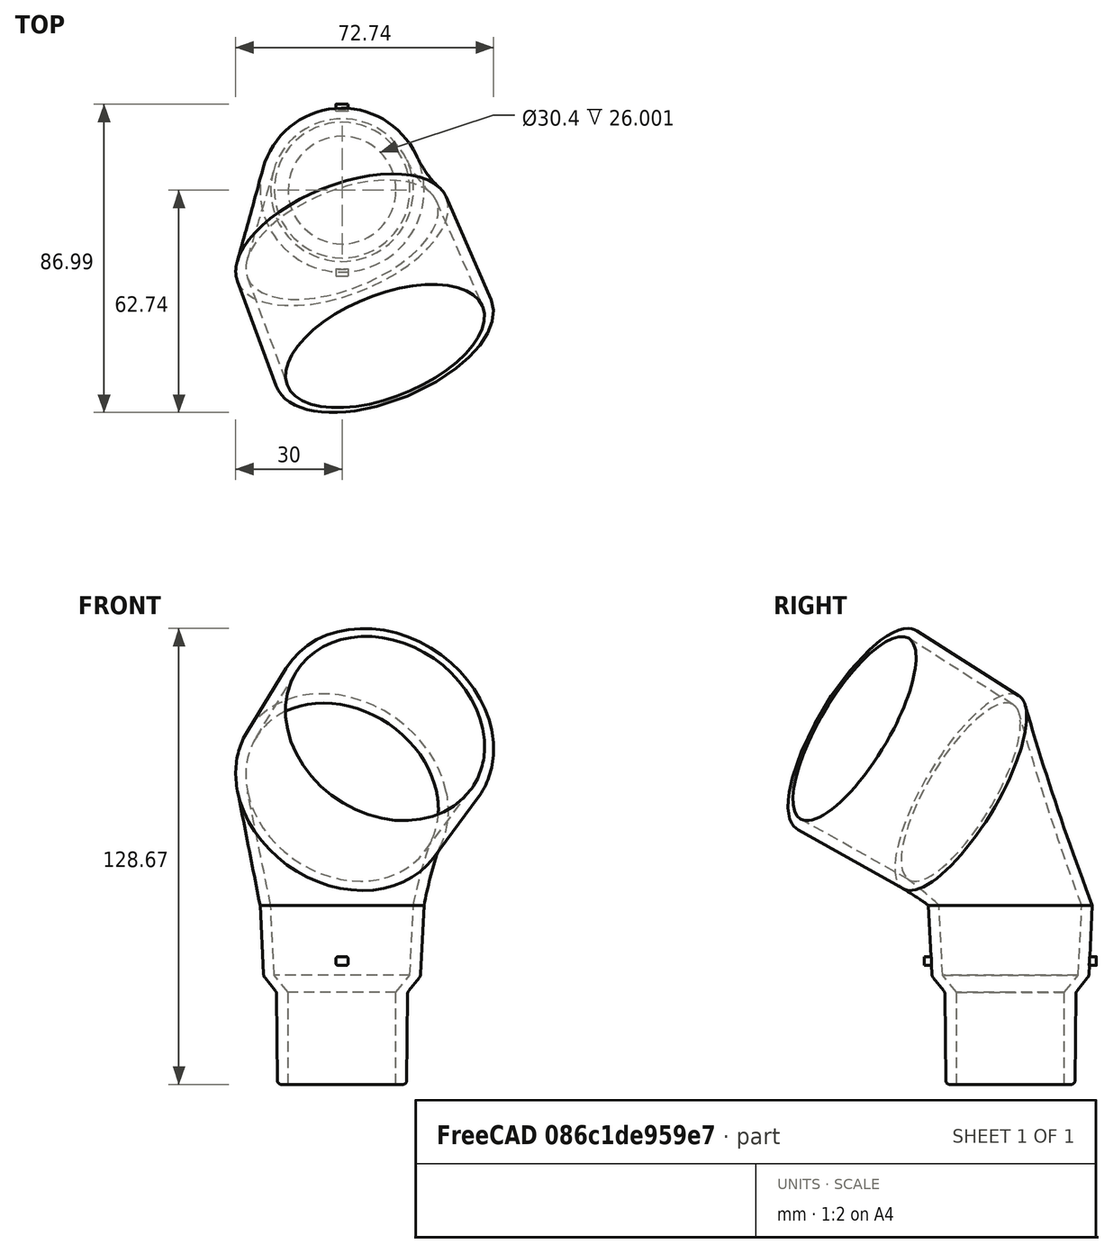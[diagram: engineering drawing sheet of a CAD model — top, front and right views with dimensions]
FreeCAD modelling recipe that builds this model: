
FCSTD DOCUMENT  (FreeCAD 1.1R20260414 (Git shallow))
Label: M18Vac
License: All rights reserved
LicenseURL: http://en.wikipedia.org/wiki/All_rights_reserved
objects: Sketcher::SketchObject×4, App::Point×2, PartDesign::Pad×2, Part::DatumPlane×2, PartDesign::Fillet×2, Spreadsheet::Sheet×1, PartDesign::Revolution×1, PartDesign::PolarPattern×1, PartDesign::AdditiveLoft×1, PartDesign::Body×1, App::Part×1, Mesh::Feature×1
note: 29 computed .brp shape members not serialized (recipe doc carries the construction recipe); baked Part::Feature solids carry a one-line shape summary decoded from their .brp

FEATURE [App::Point] Origin001
  Role = Origin
FEATURE [App::Point] Origin003
  Role = Origin
FEATURE [Sketcher::SketchObject] Sketch  label="Sketch-Plug"
  ArcFitTolerance = 1e-06
  AttachmentSupport = -> [Origin002]
  ExternalTypes = [0]
  FullyConstrained = true
  MakeInternals = false
  MapMode = 5
  Placement = pos=(0,0,0) rot=(1,0,0;1.5708rad)
  _ExternalGeoVersion = 1
  expr: Constraints[10] = Spreadsheet.Neck / 2
  expr: Constraints[16] = Spreadsheet.Thickness
  expr: Constraints[3] = 36.4 / 2
  expr: Constraints[4] = Spreadsheet.Thickness
  expr: Constraints[6] = 36.9 / 2
  expr: Constraints[8] = 44.25 / 2
  sketch-geometry (8):
    g0: LineSegment StartX=18.2 StartY=0 StartZ=0 EndX=18.45 EndY=26 EndZ=0
    g1: LineSegment StartX=22.125 StartY=30.5 StartZ=0 EndX=23.125 EndY=50.5 EndZ=0
    g2: LineSegment StartX=15.2 StartY=0 StartZ=0 EndX=18.2 EndY=0 EndZ=0
    g3: LineSegment StartX=15.2 StartY=0 StartZ=0 EndX=15.2 EndY=26.0012 EndZ=0
    g4: LineSegment StartX=19.1414 StartY=30.8274 StartZ=0 EndX=20.125 EndY=50.5 EndZ=0
    g5: LineSegment StartX=20.125 StartY=50.5 StartZ=0 EndX=23.125 EndY=50.5 EndZ=0
    g6: LineSegment StartX=15.2 StartY=26.0012 StartZ=0 EndX=19.1414 EndY=30.8274 EndZ=0
    g7: LineSegment StartX=18.45 StartY=26 StartZ=0 EndX=22.125 EndY=30.5 EndZ=0
  constraints (24):
    c: PointOnObject(g0,g-1)
    c: Coincident(g2,g0)
    c: Horizontal(g2)
    c: DistanceX(g-1,g0) = 18.2
    c: Distance(g2) = 3
    c: DistanceY(g0,g0) = 26
    c: DistanceX(g-1,g0) = 18.45
    c: DistanceY(g0,g1) = 4.5
    c: DistanceX(g-1,g1) = 22.125
    c: DistanceY(g1,g1) = 20
    c: DistanceX(g-1,g1) = 23.125
    c: Coincident(g3,g2)
    c: Vertical(g3)
    c: Coincident(g5,g1)
    c: Coincident(g4,g5)
    c: Equal(g3,g0)
    c: DistanceX(g5,g5) = 3
    c: Coincident(g6,g3)
    c: Coincident(g6,g4)
    c: Coincident(g7,g0)
    c: Coincident(g7,g1)
    c: Parallel(g1,g4)
    c: Parallel(g6,g7)
    c: Horizontal(g5)
FEATURE [Spreadsheet::Sheet] Spreadsheet
  cells = A2='Thickness; B2(Thickness)=3; A4='Neck; B4(Neck)=46.25; A9='HoseInsideDia; B9(HoseInsideDia)=57.5; A10='HoseLength; B10(HoseLength)=37
FEATURE [PartDesign::Revolution] Revolution
  Angle = 360
  Angle2 = 0
  Axis = (0,2e-16,1)
  Base = (0,0,0)
  FuseOrder = 0
  Profile = -> Sketch
  ReferenceAxis = -> Sketch [V_Axis]
  Reversed = true
  Suppressed = false
  Type = 0
FEATURE [Sketcher::SketchObject] Sketch001  label="Sketch-Pin"
  ArcFitTolerance = 1e-06
  AttachmentOffset = pos=(0,34.8,22) rot=(0,0,1;0rad)
  AttachmentSupport = -> [Origin002]
  ExternalTypes = [0]
  FullyConstrained = true
  MakeInternals = false
  MapMode = 5
  Placement = pos=(0,-22,34.8) rot=(1,0,0;1.5708rad)
  _ExternalGeoVersion = 1
  sketch-geometry (10):
    g0: LineSegment StartX=-1.75 StartY=0.55 StartZ=0 EndX=-1.75 EndY=-0.55 EndZ=0
    g1: LineSegment StartX=-1.05 StartY=-1.25 StartZ=0 EndX=1.05 EndY=-1.25 EndZ=0
    g2: LineSegment StartX=1.75 StartY=-0.55 StartZ=0 EndX=1.75 EndY=0.55 EndZ=0
    g3: LineSegment StartX=1.05 StartY=1.25 StartZ=0 EndX=-1.05 EndY=1.25 EndZ=0
    g4: ArcOfCircle CenterX=-1.05 CenterY=0.55 CenterZ=0 NormalX=0 NormalY=0 NormalZ=1 AngleXU=0 Radius=0.7 StartAngle=1.5708 EndAngle=3.14159
    g5: ArcOfCircle CenterX=-1.05 CenterY=-0.55 CenterZ=0 NormalX=0 NormalY=0 NormalZ=1 AngleXU=0 Radius=0.7 StartAngle=3.14159 EndAngle=4.71239
    g6: ArcOfCircle CenterX=1.05 CenterY=-0.55 CenterZ=0 NormalX=0 NormalY=0 NormalZ=1 AngleXU=0 Radius=0.7 StartAngle=4.71239 EndAngle=6.28319
    g7: ArcOfCircle CenterX=1.05 CenterY=0.55 CenterZ=0 NormalX=0 NormalY=0 NormalZ=1 AngleXU=0 Radius=0.7 StartAngle=0 EndAngle=1.5708
    g8: GeomPoint [constr] X=-1.75 Y=1.25 Z=0
    g9: GeomPoint [constr] X=1.75 Y=-1.25 Z=0
  constraints (22):
    c: Tangent(g0,g4) = -1.5708
    c: Tangent(g0,g5) = -1.5708
    c: Tangent(g1,g5) = -1.5708
    c: Tangent(g1,g6) = -1.5708
    c: Tangent(g2,g6) = -1.5708
    c: Tangent(g2,g7) = -1.5708
    c: Tangent(g3,g7) = -1.5708
    c: Tangent(g3,g4) = -1.5708
    c: Vertical(g0)
    c: Vertical(g2)
    c: Horizontal(g1)
    c: Horizontal(g3)
    c: Equal(g6,g7)
    c: PointOnObject(g8,g0)
    c: PointOnObject(g8,g3)
    c: PointOnObject(g9,g1)
    c: PointOnObject(g9,g2)
    c: Symmetric(g0,g2,g-2)
    c: Symmetric(g5,g4,g-1)
    c: DistanceX(g0,g2) = 3.5
    c: DistanceY(g1,g3) = 2.5
    c: Radius(g6) = 0.7
FEATURE [PartDesign::Pad] Pad
  BaseFeature = -> Revolution
  Direction = (0,-1,2e-16)
  Length = 2.25
  Length2 = 2
  Profile = -> Sketch001
  ReferenceAxis = -> Sketch001 [N_Axis]
  SideType = 0
  Suppressed = false
  Type = 0
  Type2 = 0
FEATURE [PartDesign::PolarPattern] PolarPattern
  Angle = 360
  Axis = -> Z_Axis001
  BaseFeature = -> Pad
  Mode = 0
  Occurrences = 2
  Offset = 120
  Originals = -> [Pad]
  SpacingPattern = [0]
  Spacings = [-1]
  Suppressed = false
  TransformMode = 0
FEATURE [Part::DatumPlane] DatumPlane
  AttachmentSupport = -> [PolarPattern]
  MapMode = 5
  Placement = pos=(0,1.11e-14,50.5) rot=(0,0,1;0rad)
FEATURE [Sketcher::SketchObject] Sketch002  label="Sketch-Vac"
  ArcFitTolerance = 1e-06
  AttachmentSupport = -> [DatumPlane]
  ExternalTypes = [0]
  FullyConstrained = true
  MakeInternals = false
  MapMode = 5
  Placement = pos=(0,1.11e-14,50.5) rot=(0,0,1;0rad)
  _ExternalGeoVersion = 1
  expr: Constraints[2] = Spreadsheet.Thickness
  expr: Constraints[3] = Spreadsheet.Neck
  sketch-geometry (2):
    g0: Circle CenterX=0 CenterY=0 CenterZ=0 NormalX=0 NormalY=0 NormalZ=1 AngleXU=0 Radius=23.125
    g1: Circle CenterX=0 CenterY=0 CenterZ=0 NormalX=0 NormalY=0 NormalZ=1 AngleXU=0 Radius=20.125
  constraints (4):
    c: Coincident(g0,g-1)
    c: Coincident(g1,g0)
    c: Distance(g0,g1) = 3
    c: Diameter(g0) = 46.25
FEATURE [Part::DatumPlane] DatumPlane001  label="DatumPlane-Hose"
  AttachmentOffset = pos=(0,-14,32) rot=(0.933854,0.181523,0.308165;1.12547rad)
  AttachmentSupport = -> [PolarPattern]
  MapMode = 5
  Placement = pos=(0,-14,82.5) rot=(0.933854,0.181523,0.308165;1.12547rad)
FEATURE [Sketcher::SketchObject] Sketch003  label="Sketch-Hose"
  ArcFitTolerance = 1e-06
  AttachmentSupport = -> [DatumPlane001]
  ExternalTypes = [0]
  FullyConstrained = true
  MakeInternals = false
  MapMode = 5
  Placement = pos=(0,-14,82.5) rot=(0.933854,0.181523,0.308165;1.12547rad)
  _ExternalGeoVersion = 1
  expr: Constraints[2] = Spreadsheet.Thickness
  expr: Constraints[3] = Spreadsheet.HoseInsideDia
  sketch-geometry (2):
    g0: Circle CenterX=0 CenterY=0 CenterZ=0 NormalX=0 NormalY=0 NormalZ=1 AngleXU=0 Radius=31.75
    g1: Circle CenterX=0 CenterY=0 CenterZ=0 NormalX=0 NormalY=0 NormalZ=1 AngleXU=0 Radius=28.75
  constraints (4):
    c: Coincident(g0,g-1)
    c: Coincident(g1,g0)
    c: Distance(g1,g0) = 3
    c: Diameter(g1) = 57.5
FEATURE [PartDesign::AdditiveLoft] AdditiveLoft
  BaseFeature = -> PolarPattern
  Closed = false
  Profile = -> Sketch002
  Ruled = false
  Sections = -> [Sketch003]
  Suppressed = false
FEATURE [PartDesign::Pad] Pad001
  BaseFeature = -> AdditiveLoft
  Direction = (0.327638,-0.810933,0.48481)
  Length = 37
  Length2 = 10
  Profile = -> Sketch003
  ReferenceAxis = -> Sketch003 [N_Axis]
  SideType = 0
  Suppressed = false
  TaperAngle = 1.5
  Type = 0
  Type2 = 0
  expr: Length = Spreadsheet.HoseLength
FEATURE [PartDesign::Fillet] Fillet
  Base = -> Pad001 [Edge2,Edge70]
  BaseFeature = -> Pad001
  Radius = 1
  SupportTransform = false
  Suppressed = false
  UseAllEdges = false
FEATURE [PartDesign::Fillet] Fillet001
  Base = -> Fillet [Edge8,Edge11]
  BaseFeature = -> Fillet
  Radius = 2
  SupportTransform = false
  Suppressed = false
  UseAllEdges = false
FEATURE [PartDesign::Body] Body
  AllowCompound = true
  Group = -> [Sketch,Revolution,Sketch001,Pad,PolarPattern,DatumPlane,Sketch002,DatumPlane001,Sketch003,AdditiveLoft,Pad001,Fillet,Fillet001]
  Origin = -> Origin002
  Tip = -> Fillet001
FEATURE [App::Part] Part
  Group = -> [Body]
  Origin = -> Origin
FEATURE [Mesh::Feature] Mesh  label="Fillet001 (Meshed)"
